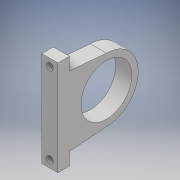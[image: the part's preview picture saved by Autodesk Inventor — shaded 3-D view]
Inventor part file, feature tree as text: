
AUTODESK INVENTOR PART (.ipt)
format: ipt  version: 2017 (Build 210142000, 142)  size: 134,656 bytes
history: native  units: mm
features: extrude x2, sketch x2
ambient origin geometry x8: Origin, YZ Plane, XZ Plane, XY Plane, X Axis, Y Axis, Z Axis, Center Point
bodies: Solid1 (feature_tree)
feature tree (4):
  extrude  "Extrusion1"  Depth=21.0mm
  extrude  "Extrusion2"  Depth=7.0mm
  sketch  "Sketch1"  dims[d0=22.0mm d1=21.0mm]
  sketch  "Sketch2"  dims[d2=90.0deg d3=21.0mm d4=180.0deg d6=27.5mm d8=5.0mm d9=90.0deg d10=5.0mm d11=90.0deg d12=7.0mm d13=0.0mm d14=3.0mm d15=7.0mm d16=0.0mm]
